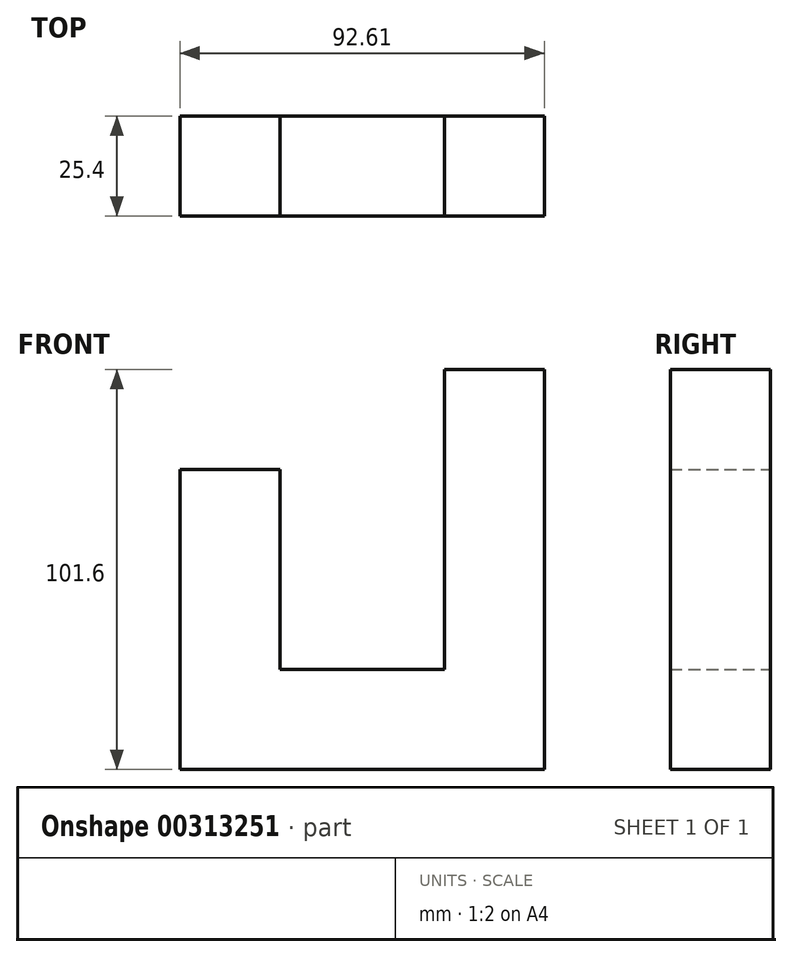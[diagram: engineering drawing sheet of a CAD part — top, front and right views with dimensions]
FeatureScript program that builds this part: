
annotation { "Feature Type Name" : "Feature", "Feature Type Description" : "" }
export const myFeature = defineFeature(function(context is Context, id is Id, definition is map)
    precondition{}
    {
        {
            var Q0;
            Q0=qCreatedBy(makeId("Front.planeOp"),FACE);
            var sketch = newSketch(context, id + "F0", { "sketchPlane" : qUnion([Q0])});
            skLineSegment(sketch, "E0", {"start": v(-46.89, -44.59) * mm, "end": v(45.72, -44.59) * mm});
            skLineSegment(sketch, "E1", {"start": v(45.72, -44.59) * mm, "end": v(45.72, 57.01) * mm});
            skLineSegment(sketch, "E2", {"start": v(45.72, 57.01) * mm, "end": v(20.32, 57.01) * mm});
            skLineSegment(sketch, "E3", {"start": v(20.32, 57.01) * mm, "end": v(20.32, -19.19) * mm});
            skLineSegment(sketch, "E4", {"start": v(20.32, -19.19) * mm, "end": v(-21.49, -19.19) * mm});
            skLineSegment(sketch, "E5", {"start": v(-21.49, -19.19) * mm, "end": v(-21.49, 31.61) * mm});
            skLineSegment(sketch, "E6", {"start": v(-21.49, 31.61) * mm, "end": v(-46.89, 31.61) * mm});
            skLineSegment(sketch, "E7", {"start": v(-46.89, 31.61) * mm, "end": v(-46.89, -44.59) * mm});
            skSolve(sketch);
        }
        {
            var Q0;
            Q0=makeQuery(id+"F0.imprint","IMPRINT",FACE,{"disambiguationData":[TD([[makeQuery(id+"F0.imprint","IMPRINT",EDGE,{"derivedFrom":sQuery(id+"F0.wireOp",EDGE,"E0")}),1.0]])]});
            extrude(context, id + "F1", {"entities" : qUnion([Q0]), "depth" : 25.4 * mm});
        }
    });
